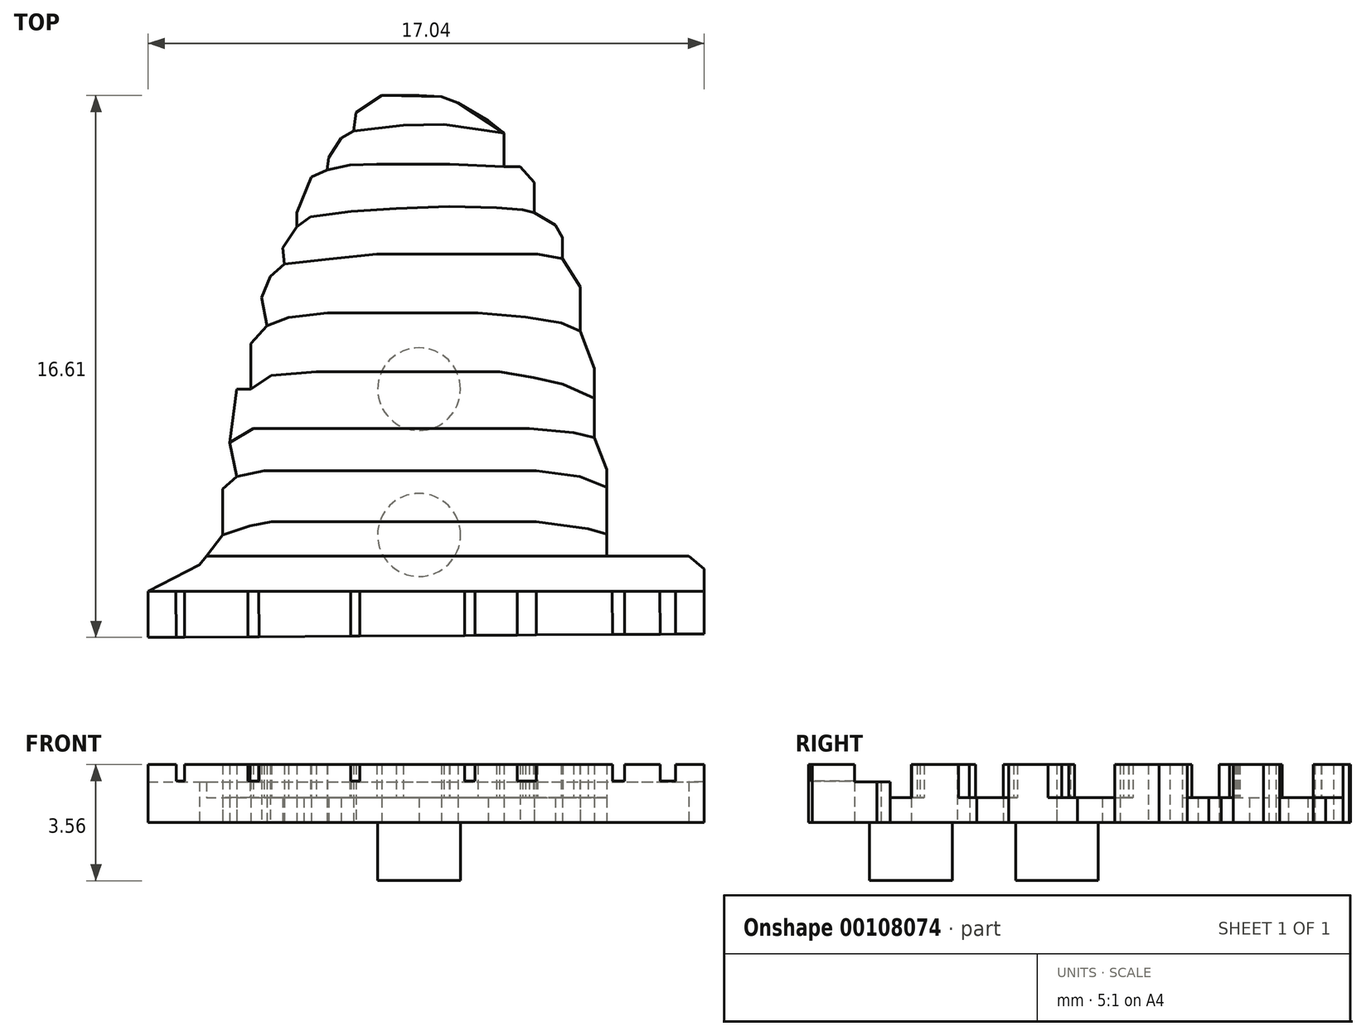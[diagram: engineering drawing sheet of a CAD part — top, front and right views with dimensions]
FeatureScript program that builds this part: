
annotation { "Feature Type Name" : "Feature", "Feature Type Description" : "" }
export const myFeature = defineFeature(function(context is Context, id is Id, definition is map)
    precondition{}
    {
        {
            var Q0;
            Q0=qCreatedBy(makeId("Top.planeOp"),FACE);
            var sketch = newSketch(context, id + "F0", { "sketchPlane" : qUnion([Q0])});
            skCircle(sketch, "E0", {"center": v(0, 0) * mm, "radius": 12.7 * mm});
            skSolve(sketch);
        }
        {
            var Q0;
            Q0=makeQuery(id+"F0.imprint","IMPRINT",FACE,{"disambiguationData":[TD([[makeQuery(id+"F0.imprint","IMPRINT",EDGE,{"derivedFrom":sQuery(id+"F0.wireOp",EDGE,"E0")}),1.0]])]});
            var sketch = newSketch(context, id + "F1", { "sketchPlane" : qUnion([Q0])});
            skLineSegment(sketch, "E1", {"start": v(-8.3, -7.61) * mm, "end": v(-8.3, -6.2) * mm});
            skLineSegment(sketch, "E2", {"start": v(-8.3, -6.2) * mm, "end": v(-6.73, -5.39) * mm});
            skLineSegment(sketch, "E3", {"start": v(-6.73, -5.39) * mm, "end": v(-6.02, -4.47) * mm});
            skLineSegment(sketch, "E4", {"start": v(-6.02, -4.47) * mm, "end": v(-6.02, -3.05) * mm});
            skLineSegment(sketch, "E5", {"start": v(-6.02, -3.05) * mm, "end": v(-5.59, -2.67) * mm});
            skLineSegment(sketch, "E6", {"start": v(-5.59, -2.67) * mm, "end": v(-5.8, -1.64) * mm});
            skLineSegment(sketch, "E7", {"start": v(-5.59, 0) * mm, "end": v(-5.15, 0) * mm});
            skLineSegment(sketch, "E8", {"start": v(-5.15, 0) * mm, "end": v(-5.15, 1.4) * mm});
            skLineSegment(sketch, "E9", {"start": v(-5.15, 1.4) * mm, "end": v(-4.67, 1.94) * mm});
            skLineSegment(sketch, "E10", {"start": v(-4.67, 1.94) * mm, "end": v(-4.83, 2.8) * mm});
            skLineSegment(sketch, "E11", {"start": v(-4.83, 2.8) * mm, "end": v(-4.56, 3.46) * mm});
            skLineSegment(sketch, "E12", {"start": v(-4.56, 3.46) * mm, "end": v(-4.12, 3.84) * mm});
            skLineSegment(sketch, "E13", {"start": v(-4.12, 3.84) * mm, "end": v(-4.18, 4.33) * mm});
            skLineSegment(sketch, "E14", {"start": v(-4.18, 4.33) * mm, "end": v(-3.74, 4.98) * mm});
            skLineSegment(sketch, "E15", {"start": v(-3.74, 4.98) * mm, "end": v(-3.74, 5.41) * mm});
            skLineSegment(sketch, "E16", {"start": v(-3.74, 5.41) * mm, "end": v(-3.53, 5.9) * mm});
            skLineSegment(sketch, "E17", {"start": v(-3.53, 5.9) * mm, "end": v(-3.3, 6.5) * mm});
            skLineSegment(sketch, "E18", {"start": v(-3.3, 6.5) * mm, "end": v(-2.82, 6.71) * mm});
            skLineSegment(sketch, "E19", {"start": v(-2.82, 6.71) * mm, "end": v(-2.77, 7.1) * mm});
            skLineSegment(sketch, "E20", {"start": v(-2.77, 7.1) * mm, "end": v(-2.39, 7.7) * mm});
            skLineSegment(sketch, "E21", {"start": v(-2.39, 7.7) * mm, "end": v(-2, 7.9) * mm});
            skLineSegment(sketch, "E22", {"start": v(-1.15, 9) * mm, "end": v(0, 9) * mm});
            skLineSegment(sketch, "E23", {"start": v(1.2, 8.78) * mm, "end": v(2.12, 8.23) * mm});
            skLineSegment(sketch, "E24", {"start": v(2.12, 8.23) * mm, "end": v(2.6, 7.85) * mm});
            skLineSegment(sketch, "E25", {"start": v(2.6, 6.82) * mm, "end": v(3.1, 6.82) * mm});
            skLineSegment(sketch, "E26", {"start": v(3.1, 6.82) * mm, "end": v(3.53, 6.33) * mm});
            skLineSegment(sketch, "E27", {"start": v(3.53, 6.33) * mm, "end": v(3.53, 5.41) * mm});
            skLineSegment(sketch, "E28", {"start": v(3.53, 5.41) * mm, "end": v(4.18, 5.03) * mm});
            skLineSegment(sketch, "E29", {"start": v(4.18, 5.03) * mm, "end": v(4.4, 4.65) * mm});
            skLineSegment(sketch, "E30", {"start": v(4.4, 4.65) * mm, "end": v(4.4, 4) * mm});
            skLineSegment(sketch, "E31", {"start": v(4.94, 3.13) * mm, "end": v(4.94, 2.48) * mm});
            skLineSegment(sketch, "E32", {"start": v(4.94, 2.48) * mm, "end": v(4.94, 1.78) * mm});
            skLineSegment(sketch, "E33", {"start": v(5.37, 0.64) * mm, "end": v(5.37, 0) * mm});
            skLineSegment(sketch, "E34", {"start": v(5.37, -1) * mm, "end": v(5.37, -1.48) * mm});
            skLineSegment(sketch, "E35", {"start": v(5.37, -1.48) * mm, "end": v(5.75, -2.46) * mm});
            skLineSegment(sketch, "E36", {"start": v(5.75, -2.46) * mm, "end": v(5.75, -2.9) * mm});
            skLineSegment(sketch, "E37", {"start": v(5.75, -2.9) * mm, "end": v(5.75, -5.11) * mm});
            skLineSegment(sketch, "E38", {"start": v(5.75, -5.11) * mm, "end": v(8.27, -5.11) * mm});
            skLineSegment(sketch, "E39", {"start": v(8.74, -5.51) * mm, "end": v(8.27, -5.11) * mm});
            skLineSegment(sketch, "E40", {"start": v(8.74, -5.51) * mm, "end": v(8.74, -7.5) * mm});
            skLineSegment(sketch, "E41", {"start": v(8.74, -7.5) * mm, "end": v(-8.3, -7.61) * mm});
            skLineSegment(sketch, "E42", {"start": v(5.37, -1) * mm, "end": v(5.37, 0) * mm});
            skLineSegment(sketch, "E43", {"start": v(5.37, 0.64) * mm, "end": v(4.94, 1.78) * mm});
            skLineSegment(sketch, "E44", {"start": v(4.94, 3.13) * mm, "end": v(4.4, 4) * mm});
            skLineSegment(sketch, "E45", {"start": v(2.6, 6.82) * mm, "end": v(2.6, 7.85) * mm});
            skLineSegment(sketch, "E46", {"start": v(-1.15, 9) * mm, "end": v(-1.93, 8.48) * mm});
            skLineSegment(sketch, "E47", {"start": v(-1.93, 8.48) * mm, "end": v(-2, 7.9) * mm});
            skLineSegment(sketch, "E48", {"start": v(1.2, 8.78) * mm, "end": v(0.69, 8.96) * mm});
            skLineSegment(sketch, "E49", {"start": v(0, 9) * mm, "end": v(0.69, 8.96) * mm});
            skLineSegment(sketch, "E50", {"start": v(-5.59, 0) * mm, "end": v(-5.8, -1.64) * mm});
            skSolve(sketch);
        }
        {
            var Q0;
            Q0 = qSketchRegion(id + "F1", true);
            extrude(context, id + "F2", {"entities" : qUnion([Q0]), "depth" : 0.76 * mm});
        }
        {
            var Q0;
            Q0=makeQuery(id+"F2.opExtrude","CAP_FACE",FACE,{"disambiguationData":[OSD([sQuery(id+"F1.wireOp",EDGE,"E1"),sQuery(id+"F1.wireOp",EDGE,"E2"),sQuery(id+"F1.wireOp",EDGE,"E3"),sQuery(id+"F1.wireOp",EDGE,"E4"),sQuery(id+"F1.wireOp",EDGE,"E5"),sQuery(id+"F1.wireOp",EDGE,"E6"),sQuery(id+"F1.wireOp",EDGE,"E7"),sQuery(id+"F1.wireOp",EDGE,"E8"),sQuery(id+"F1.wireOp",EDGE,"E9"),sQuery(id+"F1.wireOp",EDGE,"E10"),sQuery(id+"F1.wireOp",EDGE,"E11"),sQuery(id+"F1.wireOp",EDGE,"E12"),sQuery(id+"F1.wireOp",EDGE,"E13"),sQuery(id+"F1.wireOp",EDGE,"E14"),sQuery(id+"F1.wireOp",EDGE,"E15"),sQuery(id+"F1.wireOp",EDGE,"E16"),sQuery(id+"F1.wireOp",EDGE,"E17"),sQuery(id+"F1.wireOp",EDGE,"E18"),sQuery(id+"F1.wireOp",EDGE,"E19"),sQuery(id+"F1.wireOp",EDGE,"E20"),sQuery(id+"F1.wireOp",EDGE,"E21"),sQuery(id+"F1.wireOp",EDGE,"E22"),sQuery(id+"F1.wireOp",EDGE,"E23"),sQuery(id+"F1.wireOp",EDGE,"E24"),sQuery(id+"F1.wireOp",EDGE,"E25"),sQuery(id+"F1.wireOp",EDGE,"E26"),sQuery(id+"F1.wireOp",EDGE,"E27"),sQuery(id+"F1.wireOp",EDGE,"E28"),sQuery(id+"F1.wireOp",EDGE,"E29"),sQuery(id+"F1.wireOp",EDGE,"E30"),sQuery(id+"F1.wireOp",EDGE,"E31"),sQuery(id+"F1.wireOp",EDGE,"E32"),sQuery(id+"F1.wireOp",EDGE,"E33"),sQuery(id+"F1.wireOp",EDGE,"E34"),sQuery(id+"F1.wireOp",EDGE,"E35"),sQuery(id+"F1.wireOp",EDGE,"E36"),sQuery(id+"F1.wireOp",EDGE,"E37"),sQuery(id+"F1.wireOp",EDGE,"E38"),sQuery(id+"F1.wireOp",EDGE,"E39"),sQuery(id+"F1.wireOp",EDGE,"E40"),sQuery(id+"F1.wireOp",EDGE,"E41"),sQuery(id+"F1.wireOp",EDGE,"E42"),sQuery(id+"F1.wireOp",EDGE,"E43"),sQuery(id+"F1.wireOp",EDGE,"E44"),sQuery(id+"F1.wireOp",EDGE,"E45"),sQuery(id+"F1.wireOp",EDGE,"E46"),sQuery(id+"F1.wireOp",EDGE,"E47"),sQuery(id+"F1.wireOp",EDGE,"E48"),sQuery(id+"F1.wireOp",EDGE,"E49"),sQuery(id+"F1.wireOp",EDGE,"E50")])],"isStart":false});
            var sketch = newSketch(context, id + "F3", { "sketchPlane" : qUnion([Q0])});
            skLineSegment(sketch, "E51", {"start": v(8.74, -7.5) * mm, "end": v(8.74, -5.51) * mm});
            skLineSegment(sketch, "E52", {"start": v(8.74, -5.51) * mm, "end": v(8.27, -5.11) * mm});
            skLineSegment(sketch, "E53", {"start": v(8.27, -5.11) * mm, "end": v(5.75, -5.11) * mm});
            skLineSegment(sketch, "E54", {"start": v(5.75, -5.11) * mm, "end": v(-6.52, -5.11) * mm});
            skLineSegment(sketch, "E55", {"start": v(-6.52, -5.11) * mm, "end": v(-6.73, -5.39) * mm});
            skLineSegment(sketch, "E56", {"start": v(-6.73, -5.39) * mm, "end": v(-8.3, -6.2) * mm});
            skLineSegment(sketch, "E57", {"start": v(-8.3, -6.2) * mm, "end": v(-8.3, -7.61) * mm});
            skLineSegment(sketch, "E58", {"start": v(-8.3, -7.61) * mm, "end": v(8.74, -7.5) * mm});
            skSolve(sketch);
        }
        {
            var Q0;
            Q0 = qSketchRegion(id + "F3", true);
            extrude(context, id + "F4", {"entities" : qUnion([Q0]), "operationType" : NewBodyOperationType.ADD, "depth" : 1.02 * mm});
        }
        {
            var Q0;
            Q0=makeQuery(id+"F2.opExtrude","CAP_FACE",FACE,{"disambiguationData":[OSD([sQuery(id+"F1.wireOp",EDGE,"E1"),sQuery(id+"F1.wireOp",EDGE,"E2"),sQuery(id+"F1.wireOp",EDGE,"E3"),sQuery(id+"F1.wireOp",EDGE,"E4"),sQuery(id+"F1.wireOp",EDGE,"E5"),sQuery(id+"F1.wireOp",EDGE,"E6"),sQuery(id+"F1.wireOp",EDGE,"E7"),sQuery(id+"F1.wireOp",EDGE,"E8"),sQuery(id+"F1.wireOp",EDGE,"E9"),sQuery(id+"F1.wireOp",EDGE,"E10"),sQuery(id+"F1.wireOp",EDGE,"E11"),sQuery(id+"F1.wireOp",EDGE,"E12"),sQuery(id+"F1.wireOp",EDGE,"E13"),sQuery(id+"F1.wireOp",EDGE,"E14"),sQuery(id+"F1.wireOp",EDGE,"E15"),sQuery(id+"F1.wireOp",EDGE,"E16"),sQuery(id+"F1.wireOp",EDGE,"E17"),sQuery(id+"F1.wireOp",EDGE,"E18"),sQuery(id+"F1.wireOp",EDGE,"E19"),sQuery(id+"F1.wireOp",EDGE,"E20"),sQuery(id+"F1.wireOp",EDGE,"E21"),sQuery(id+"F1.wireOp",EDGE,"E22"),sQuery(id+"F1.wireOp",EDGE,"E23"),sQuery(id+"F1.wireOp",EDGE,"E24"),sQuery(id+"F1.wireOp",EDGE,"E25"),sQuery(id+"F1.wireOp",EDGE,"E26"),sQuery(id+"F1.wireOp",EDGE,"E27"),sQuery(id+"F1.wireOp",EDGE,"E28"),sQuery(id+"F1.wireOp",EDGE,"E29"),sQuery(id+"F1.wireOp",EDGE,"E30"),sQuery(id+"F1.wireOp",EDGE,"E31"),sQuery(id+"F1.wireOp",EDGE,"E32"),sQuery(id+"F1.wireOp",EDGE,"E33"),sQuery(id+"F1.wireOp",EDGE,"E34"),sQuery(id+"F1.wireOp",EDGE,"E35"),sQuery(id+"F1.wireOp",EDGE,"E36"),sQuery(id+"F1.wireOp",EDGE,"E37"),sQuery(id+"F1.wireOp",EDGE,"E38"),sQuery(id+"F1.wireOp",EDGE,"E39"),sQuery(id+"F1.wireOp",EDGE,"E40"),sQuery(id+"F1.wireOp",EDGE,"E41"),sQuery(id+"F1.wireOp",EDGE,"E42"),sQuery(id+"F1.wireOp",EDGE,"E43"),sQuery(id+"F1.wireOp",EDGE,"E44"),sQuery(id+"F1.wireOp",EDGE,"E45"),sQuery(id+"F1.wireOp",EDGE,"E46"),sQuery(id+"F1.wireOp",EDGE,"E47"),sQuery(id+"F1.wireOp",EDGE,"E48"),sQuery(id+"F1.wireOp",EDGE,"E49"),sQuery(id+"F1.wireOp",EDGE,"E50")])],"isStart":false});
            var sketch = newSketch(context, id + "F5", { "sketchPlane" : qUnion([Q0])});
            skLineSegment(sketch, "E59", {"start": v(-2, 7.9) * mm, "end": v(-0.48, 8.1) * mm});
            skLineSegment(sketch, "E60", {"start": v(-0.48, 8.1) * mm, "end": v(0.77, 8.11) * mm});
            skLineSegment(sketch, "E61", {"start": v(0.77, 8.11) * mm, "end": v(2.6, 7.85) * mm});
            skLineSegment(sketch, "E62", {"start": v(2.6, 7.85) * mm, "end": v(1.2, 8.78) * mm});
            skLineSegment(sketch, "E63", {"start": v(1.2, 8.78) * mm, "end": v(0.69, 8.96) * mm});
            skLineSegment(sketch, "E64", {"start": v(0.69, 8.96) * mm, "end": v(-1.15, 9) * mm});
            skLineSegment(sketch, "E65", {"start": v(-1.15, 9) * mm, "end": v(-1.93, 8.48) * mm});
            skLineSegment(sketch, "E66", {"start": v(-1.93, 8.48) * mm, "end": v(-2, 7.9) * mm});
            skLineSegment(sketch, "E67", {"start": v(-2.82, 6.71) * mm, "end": v(-2.12, 6.87) * mm});
            skLineSegment(sketch, "E68", {"start": v(-2.12, 6.87) * mm, "end": v(-1.3, 6.9) * mm});
            skLineSegment(sketch, "E69", {"start": v(-1.3, 6.9) * mm, "end": v(0.94, 6.9) * mm});
            skLineSegment(sketch, "E70", {"start": v(0.94, 6.9) * mm, "end": v(2.6, 6.82) * mm});
            skLineSegment(sketch, "E71", {"start": v(2.6, 6.82) * mm, "end": v(3.1, 6.82) * mm});
            skLineSegment(sketch, "E72", {"start": v(3.1, 6.82) * mm, "end": v(3.53, 6.33) * mm});
            skLineSegment(sketch, "E73", {"start": v(3.53, 6.33) * mm, "end": v(3.53, 5.41) * mm});
            skLineSegment(sketch, "E74", {"start": v(3.53, 5.41) * mm, "end": v(3.18, 5.5) * mm});
            skLineSegment(sketch, "E75", {"start": v(3.18, 5.5) * mm, "end": v(2.38, 5.56) * mm});
            skLineSegment(sketch, "E76", {"start": v(2.38, 5.56) * mm, "end": v(0.93, 5.6) * mm});
            skLineSegment(sketch, "E77", {"start": v(0.93, 5.6) * mm, "end": v(-0.7, 5.54) * mm});
            skLineSegment(sketch, "E78", {"start": v(-0.7, 5.54) * mm, "end": v(-2.09, 5.45) * mm});
            skLineSegment(sketch, "E79", {"start": v(-2.09, 5.45) * mm, "end": v(-3.33, 5.29) * mm});
            skLineSegment(sketch, "E80", {"start": v(-3.33, 5.29) * mm, "end": v(-3.74, 4.98) * mm});
            skLineSegment(sketch, "E81", {"start": v(-3.74, 4.98) * mm, "end": v(-3.74, 5.41) * mm});
            skLineSegment(sketch, "E82", {"start": v(-3.74, 5.41) * mm, "end": v(-3.3, 6.5) * mm});
            skLineSegment(sketch, "E83", {"start": v(-3.3, 6.5) * mm, "end": v(-2.82, 6.71) * mm});
            skLineSegment(sketch, "E84", {"start": v(-4.12, 3.84) * mm, "end": v(-2.76, 3.99) * mm});
            skLineSegment(sketch, "E85", {"start": v(-2.76, 3.99) * mm, "end": v(-1.3, 4.14) * mm});
            skLineSegment(sketch, "E86", {"start": v(-1.3, 4.14) * mm, "end": v(0.85, 4.14) * mm});
            skLineSegment(sketch, "E87", {"start": v(0.85, 4.14) * mm, "end": v(2.4, 4.14) * mm});
            skLineSegment(sketch, "E88", {"start": v(2.4, 4.14) * mm, "end": v(3.63, 4.14) * mm});
            skLineSegment(sketch, "E89", {"start": v(3.63, 4.14) * mm, "end": v(4.4, 4) * mm});
            skLineSegment(sketch, "E90", {"start": v(4.4, 4) * mm, "end": v(4.94, 3.13) * mm});
            skLineSegment(sketch, "E91", {"start": v(4.94, 3.13) * mm, "end": v(4.94, 1.78) * mm});
            skLineSegment(sketch, "E92", {"start": v(4.94, 1.78) * mm, "end": v(4.36, 2.04) * mm});
            skLineSegment(sketch, "E93", {"start": v(4.36, 2.04) * mm, "end": v(3.26, 2.2) * mm});
            skLineSegment(sketch, "E94", {"start": v(3.26, 2.2) * mm, "end": v(1.8, 2.33) * mm});
            skLineSegment(sketch, "E95", {"start": v(1.8, 2.33) * mm, "end": v(0.16, 2.33) * mm});
            skLineSegment(sketch, "E96", {"start": v(0.16, 2.33) * mm, "end": v(-1.31, 2.33) * mm});
            skLineSegment(sketch, "E97", {"start": v(-1.31, 2.33) * mm, "end": v(-2.8, 2.33) * mm});
            skLineSegment(sketch, "E98", {"start": v(-2.8, 2.33) * mm, "end": v(-4, 2.2) * mm});
            skLineSegment(sketch, "E99", {"start": v(-4, 2.2) * mm, "end": v(-4.67, 1.94) * mm});
            skLineSegment(sketch, "E100", {"start": v(-4.67, 1.94) * mm, "end": v(-4.83, 2.8) * mm});
            skLineSegment(sketch, "E101", {"start": v(-4.83, 2.8) * mm, "end": v(-4.56, 3.46) * mm});
            skLineSegment(sketch, "E102", {"start": v(-4.56, 3.46) * mm, "end": v(-4.12, 3.84) * mm});
            skLineSegment(sketch, "E103", {"start": v(-5.8, -1.64) * mm, "end": v(-5.59, 0) * mm});
            skLineSegment(sketch, "E104", {"start": v(-5.59, 0) * mm, "end": v(-5.15, 0) * mm});
            skLineSegment(sketch, "E105", {"start": v(-5.15, 0) * mm, "end": v(-4.53, 0.42) * mm});
            skLineSegment(sketch, "E106", {"start": v(-4.53, 0.42) * mm, "end": v(-3.15, 0.54) * mm});
            skLineSegment(sketch, "E107", {"start": v(-3.15, 0.54) * mm, "end": v(0, 0.54) * mm});
            skLineSegment(sketch, "E108", {"start": v(0, 0.54) * mm, "end": v(2.47, 0.54) * mm});
            skLineSegment(sketch, "E109", {"start": v(2.47, 0.54) * mm, "end": v(3.5, 0.36) * mm});
            skLineSegment(sketch, "E110", {"start": v(3.5, 0.36) * mm, "end": v(4.41, 0.15) * mm});
            skLineSegment(sketch, "E111", {"start": v(4.41, 0.15) * mm, "end": v(5.37, -0.27) * mm});
            skLineSegment(sketch, "E112", {"start": v(5.37, -0.27) * mm, "end": v(5.37, -1.48) * mm});
            skLineSegment(sketch, "E113", {"start": v(5.37, -1.48) * mm, "end": v(4.74, -1.33) * mm});
            skLineSegment(sketch, "E114", {"start": v(4.74, -1.33) * mm, "end": v(3.37, -1.2) * mm});
            skLineSegment(sketch, "E115", {"start": v(3.37, -1.2) * mm, "end": v(0.9, -1.2) * mm});
            skLineSegment(sketch, "E116", {"start": v(0.9, -1.2) * mm, "end": v(-1.5, -1.2) * mm});
            skLineSegment(sketch, "E117", {"start": v(-1.5, -1.2) * mm, "end": v(-3.98, -1.2) * mm});
            skLineSegment(sketch, "E118", {"start": v(-3.98, -1.2) * mm, "end": v(-5.08, -1.2) * mm});
            skLineSegment(sketch, "E119", {"start": v(-5.08, -1.2) * mm, "end": v(-5.8, -1.64) * mm});
            skLineSegment(sketch, "E120", {"start": v(-6.02, -3.05) * mm, "end": v(-5.59, -2.67) * mm});
            skLineSegment(sketch, "E121", {"start": v(-5.59, -2.67) * mm, "end": v(-4.75, -2.5) * mm});
            skLineSegment(sketch, "E122", {"start": v(-4.75, -2.5) * mm, "end": v(-2.44, -2.5) * mm});
            skLineSegment(sketch, "E123", {"start": v(-2.44, -2.5) * mm, "end": v(1.34, -2.5) * mm});
            skLineSegment(sketch, "E124", {"start": v(1.34, -2.5) * mm, "end": v(3.6, -2.5) * mm});
            skLineSegment(sketch, "E125", {"start": v(3.6, -2.5) * mm, "end": v(4.92, -2.68) * mm});
            skLineSegment(sketch, "E126", {"start": v(4.92, -2.68) * mm, "end": v(5.75, -3.02) * mm});
            skLineSegment(sketch, "E127", {"start": v(5.75, -3.02) * mm, "end": v(5.75, -4.45) * mm});
            skLineSegment(sketch, "E128", {"start": v(5.75, -4.45) * mm, "end": v(5.18, -4.28) * mm});
            skLineSegment(sketch, "E129", {"start": v(5.18, -4.28) * mm, "end": v(3.6, -4.07) * mm});
            skLineSegment(sketch, "E130", {"start": v(3.6, -4.07) * mm, "end": v(1.46, -4.07) * mm});
            skLineSegment(sketch, "E131", {"start": v(1.46, -4.07) * mm, "end": v(-2, -4.07) * mm});
            skLineSegment(sketch, "E132", {"start": v(-2, -4.07) * mm, "end": v(-4.52, -4.07) * mm});
            skLineSegment(sketch, "E133", {"start": v(-4.52, -4.07) * mm, "end": v(-5.18, -4.2) * mm});
            skLineSegment(sketch, "E134", {"start": v(-5.18, -4.2) * mm, "end": v(-6.02, -4.47) * mm});
            skLineSegment(sketch, "E135", {"start": v(-6.02, -4.47) * mm, "end": v(-6.02, -3.05) * mm});
            skSolve(sketch);
        }
        {
            var Q0;
            Q0 = qSketchRegion(id + "F5", true);
            extrude(context, id + "F6", {"entities" : qUnion([Q0]), "operationType" : NewBodyOperationType.ADD, "depth" : 1.02 * mm});
        }
        {
            var Q0;
            Q0=makeQuery(id+"F4.opExtrude","CAP_FACE",FACE,{"disambiguationData":[OSD([sQuery(id+"F3.wireOp",EDGE,"E51"),sQuery(id+"F3.wireOp",EDGE,"E52"),sQuery(id+"F3.wireOp",EDGE,"E53"),sQuery(id+"F3.wireOp",EDGE,"E54"),sQuery(id+"F3.wireOp",EDGE,"E55"),sQuery(id+"F3.wireOp",EDGE,"E56"),sQuery(id+"F3.wireOp",EDGE,"E57"),sQuery(id+"F3.wireOp",EDGE,"E58")])],"isStart":false});
            var sketch = newSketch(context, id + "F7", { "sketchPlane" : qUnion([Q0])});
            skLineSegment(sketch, "E136", {"start": v(-8.3, -6.2) * mm, "end": v(-6.73, -5.39) * mm});
            skLineSegment(sketch, "E137", {"start": v(-6.73, -5.39) * mm, "end": v(-6.52, -5.11) * mm});
            skLineSegment(sketch, "E138", {"start": v(-6.52, -5.11) * mm, "end": v(8.27, -5.11) * mm});
            skLineSegment(sketch, "E139", {"start": v(8.27, -5.11) * mm, "end": v(8.74, -5.51) * mm});
            skLineSegment(sketch, "E140", {"start": v(-8.3, -6.2) * mm, "end": v(8.74, -6.2) * mm});
            skLineSegment(sketch, "E141", {"start": v(8.74, -6.2) * mm, "end": v(8.74, -5.51) * mm});
            skSolve(sketch);
        }
        {
            var Q0;
            Q0 = qSketchRegion(id + "F7", true);
            extrude(context, id + "F8", {"entities" : qUnion([Q0]), "operationType" : NewBodyOperationType.REMOVE, "oppositeDirection" : true, "depth" : 0.53 * mm});
        }
        {
            var Q0;
            Q0=makeQuery(id+"F4.opExtrude","CAP_FACE",FACE,{"disambiguationData":[OSD([sQuery(id+"F3.wireOp",EDGE,"E51"),sQuery(id+"F3.wireOp",EDGE,"E52"),sQuery(id+"F3.wireOp",EDGE,"E53"),sQuery(id+"F3.wireOp",EDGE,"E54"),sQuery(id+"F3.wireOp",EDGE,"E55"),sQuery(id+"F3.wireOp",EDGE,"E56"),sQuery(id+"F3.wireOp",EDGE,"E57"),sQuery(id+"F3.wireOp",EDGE,"E58")])],"isStart":false});
            var sketch = newSketch(context, id + "F9", { "sketchPlane" : qUnion([Q0])});
            skLineSegment(sketch, "E142", {"start": v(-7.44, -7.6) * mm, "end": v(-7.45, -6.2) * mm});
            skLineSegment(sketch, "E143", {"start": v(-7.45, -6.2) * mm, "end": v(-7.19, -6.2) * mm});
            skLineSegment(sketch, "E144", {"start": v(-7.19, -6.2) * mm, "end": v(-7.19, -7.6) * mm});
            skLineSegment(sketch, "E145", {"start": v(-7.19, -7.6) * mm, "end": v(-7.44, -7.6) * mm});
            skLineSegment(sketch, "E146", {"start": v(-5.25, -6.2) * mm, "end": v(-5.25, -7.6) * mm});
            skLineSegment(sketch, "E147", {"start": v(-5.25, -7.6) * mm, "end": v(-4.9, -7.6) * mm});
            skLineSegment(sketch, "E148", {"start": v(-4.9, -7.6) * mm, "end": v(-4.91, -6.2) * mm});
            skLineSegment(sketch, "E149", {"start": v(-4.91, -6.2) * mm, "end": v(-5.25, -6.2) * mm});
            skLineSegment(sketch, "E150", {"start": v(-2.1, -6.2) * mm, "end": v(-2.1, -7.57) * mm});
            skLineSegment(sketch, "E151", {"start": v(-2.1, -7.57) * mm, "end": v(-1.81, -7.57) * mm});
            skLineSegment(sketch, "E152", {"start": v(-1.81, -7.57) * mm, "end": v(-1.82, -6.2) * mm});
            skLineSegment(sketch, "E153", {"start": v(-1.82, -6.2) * mm, "end": v(-2.1, -6.2) * mm});
            skLineSegment(sketch, "E154", {"start": v(7.87, -6.2) * mm, "end": v(7.87, -7.5) * mm});
            skLineSegment(sketch, "E155", {"start": v(7.87, -7.5) * mm, "end": v(7.39, -7.51) * mm});
            skLineSegment(sketch, "E156", {"start": v(7.39, -7.51) * mm, "end": v(7.38, -6.2) * mm});
            skLineSegment(sketch, "E157", {"start": v(7.38, -6.2) * mm, "end": v(7.87, -6.2) * mm});
            skLineSegment(sketch, "E158", {"start": v(6.3, -6.2) * mm, "end": v(6.3, -7.52) * mm});
            skLineSegment(sketch, "E159", {"start": v(6.3, -7.52) * mm, "end": v(5.93, -7.52) * mm});
            skLineSegment(sketch, "E160", {"start": v(5.93, -7.52) * mm, "end": v(5.92, -6.2) * mm});
            skLineSegment(sketch, "E161", {"start": v(5.92, -6.2) * mm, "end": v(6.3, -6.2) * mm});
            skLineSegment(sketch, "E162", {"start": v(3.6, -7.54) * mm, "end": v(3.59, -6.2) * mm});
            skLineSegment(sketch, "E163", {"start": v(3.59, -6.2) * mm, "end": v(3.01, -6.2) * mm});
            skLineSegment(sketch, "E164", {"start": v(3.01, -6.2) * mm, "end": v(3.01, -7.54) * mm});
            skLineSegment(sketch, "E165", {"start": v(3.01, -7.54) * mm, "end": v(3.6, -7.54) * mm});
            skLineSegment(sketch, "E166", {"start": v(1.7, -6.2) * mm, "end": v(1.72, -7.55) * mm});
            skLineSegment(sketch, "E167", {"start": v(1.72, -7.55) * mm, "end": v(1.4, -7.55) * mm});
            skLineSegment(sketch, "E168", {"start": v(1.4, -7.55) * mm, "end": v(1.4, -6.2) * mm});
            skLineSegment(sketch, "E169", {"start": v(1.4, -6.2) * mm, "end": v(1.7, -6.2) * mm});
            skSolve(sketch);
        }
        {
            var Q0;
            Q0=makeQuery(id+"F9.imprint","IMPRINT",FACE,{"disambiguationData":[TD([[makeQuery(id+"F9.imprint","IMPRINT",EDGE,{"derivedFrom":sQuery(id+"F9.wireOp",EDGE,"E142")}),-1.0]])]});
            var Q1;
            Q1=makeQuery(id+"F9.imprint","IMPRINT",FACE,{"disambiguationData":[TD([[makeQuery(id+"F9.imprint","IMPRINT",EDGE,{"derivedFrom":sQuery(id+"F9.wireOp",EDGE,"E146")}),1.0]])]});
            var Q2;
            Q2=makeQuery(id+"F9.imprint","IMPRINT",FACE,{"disambiguationData":[TD([[makeQuery(id+"F9.imprint","IMPRINT",EDGE,{"derivedFrom":sQuery(id+"F9.wireOp",EDGE,"E150")}),1.0]])]});
            var Q3;
            Q3=makeQuery(id+"F9.imprint","IMPRINT",FACE,{"disambiguationData":[TD([[makeQuery(id+"F9.imprint","IMPRINT",EDGE,{"derivedFrom":sQuery(id+"F9.wireOp",EDGE,"E154")}),-1.0]])]});
            var Q4;
            Q4=makeQuery(id+"F9.imprint","IMPRINT",FACE,{"disambiguationData":[TD([[makeQuery(id+"F9.imprint","IMPRINT",EDGE,{"derivedFrom":sQuery(id+"F9.wireOp",EDGE,"E158")}),-1.0]])]});
            var Q5;
            Q5=makeQuery(id+"F9.imprint","IMPRINT",FACE,{"disambiguationData":[TD([[makeQuery(id+"F9.imprint","IMPRINT",EDGE,{"derivedFrom":sQuery(id+"F9.wireOp",EDGE,"E162")}),1.0]])]});
            var Q6;
            Q6=makeQuery(id+"F9.imprint","IMPRINT",FACE,{"disambiguationData":[TD([[makeQuery(id+"F9.imprint","IMPRINT",EDGE,{"derivedFrom":sQuery(id+"F9.wireOp",EDGE,"E166")}),-1.0]])]});
            var Q7;
            Q7=makeQuery(id+"F0.imprint","IMPRINT",FACE,{"disambiguationData":[TD([[makeQuery(id+"F0.imprint","IMPRINT",EDGE,{"derivedFrom":sQuery(id+"F0.wireOp",EDGE,"E0")}),1.0]])]});
            extrude(context, id + "F10", {"entities" : qUnion([Q0, Q1, Q2, Q3, Q4, Q5, Q6, Q7]), "operationType" : NewBodyOperationType.REMOVE, "oppositeDirection" : true, "depth" : 0.5 * mm});
        }
        {
            var Q0;
            Q0=makeQuery(id+"F0.imprint","IMPRINT",FACE,{"disambiguationData":[TD([[makeQuery(id+"F0.imprint","IMPRINT",EDGE,{"derivedFrom":sQuery(id+"F0.wireOp",EDGE,"E0")}),1.0]])]});
            var sketch = newSketch(context, id + "F11", { "sketchPlane" : qUnion([Q0])});
            skCircle(sketch, "E170", {"center": v(0, 0) * mm, "radius": 1.27 * mm});
            skCircle(sketch, "E171", {"center": v(0, -4.47) * mm, "radius": 1.27 * mm});
            skSolve(sketch);
        }
        {
            var Q0;
            Q0 = qSketchRegion(id + "F11", true);
            extrude(context, id + "F12", {"entities" : qUnion([Q0]), "operationType" : NewBodyOperationType.ADD, "oppositeDirection" : true, "depth" : 1.78 * mm});
        }
    });
